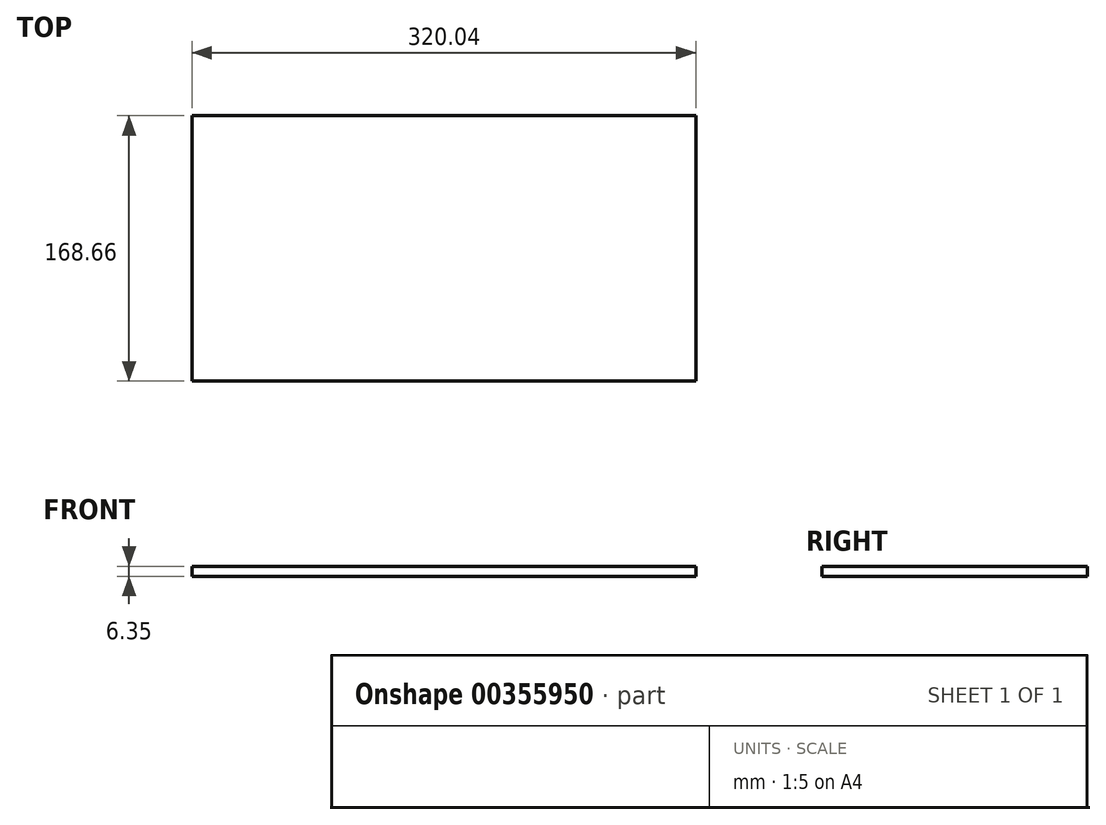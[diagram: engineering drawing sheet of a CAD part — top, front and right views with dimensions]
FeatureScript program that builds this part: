
annotation { "Feature Type Name" : "Feature", "Feature Type Description" : "" }
export const myFeature = defineFeature(function(context is Context, id is Id, definition is map)
    precondition{}
    {
        {
            var Q0;
            Q0=qCreatedBy(makeId("Top.planeOp"),FACE);
            var sketch = newSketch(context, id + "F0", { "sketchPlane" : qUnion([Q0])});
            skLineSegment(sketch, "E0.bottom", {"start": v(160.02, -84.33) * mm, "end": v(-160.02, -84.33) * mm});
            skLineSegment(sketch, "E0.top", {"start": v(160.02, 84.33) * mm, "end": v(-160.02, 84.33) * mm});
            skLineSegment(sketch, "E0.left", {"start": v(160.02, -84.33) * mm, "end": v(160.02, 84.33) * mm});
            skLineSegment(sketch, "E0.right", {"start": v(-160.02, -84.33) * mm, "end": v(-160.02, 84.33) * mm});
            skPoint(sketch, "E0.middle", {"position": v(0, 0) * mm});
            skSolve(sketch);
        }
        {
            var Q0;
            Q0=qSketchRegion(id+"F0",true);
            extrude(context, id + "F1", {"entities" : qUnion([Q0]), "depth" : 6.35 * mm});
        }
    });
